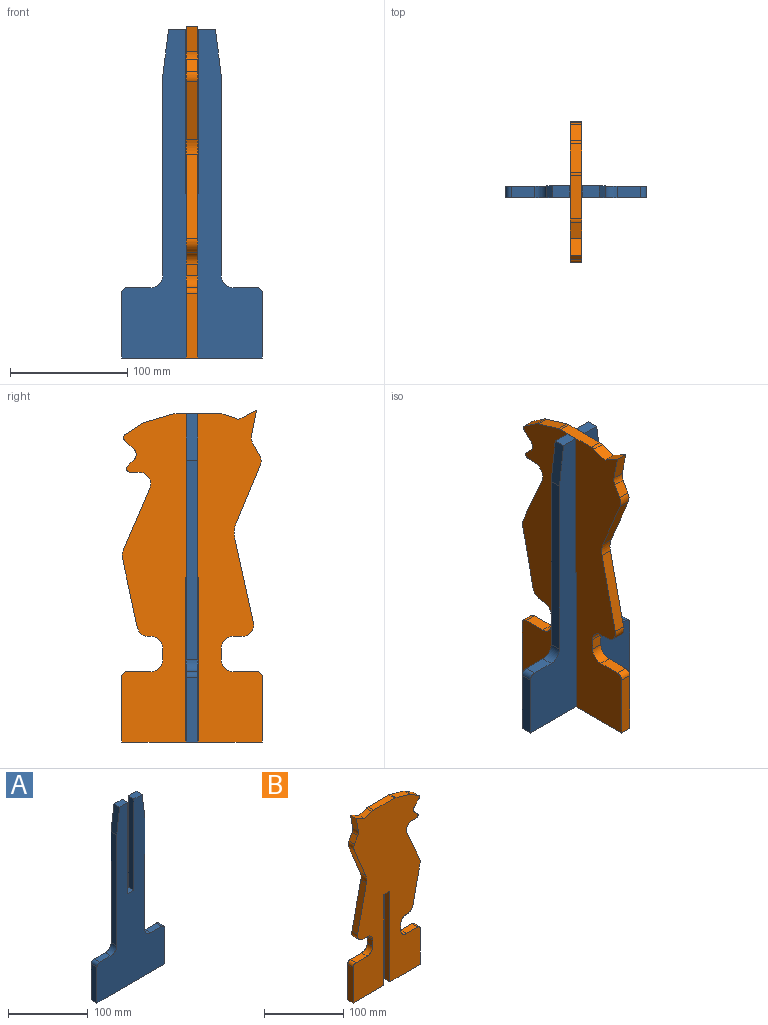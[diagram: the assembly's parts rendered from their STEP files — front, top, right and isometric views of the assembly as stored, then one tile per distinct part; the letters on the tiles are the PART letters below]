
ASSEMBLY  parts=2 mates=1
PART A: 20 faces, bbox 120x10x280 mm
  f0: plane 170x10mm, normal (-1,0,0), area 1700mm2, adj f1,f17,f18,f19
  f1: cylinder r=10mm len=10mm, axis (0,-1,0), area 157.1mm2, adj f0,f2,f18,f19
  f2: plane 20x10mm, normal (0,0,1), area 200mm2, adj f1,f3,f18,f19
  f3: cylinder r=5mm len=10mm, axis (0,-1,0), area 78.5mm2, adj f2,f4,f18,f19
  f4: plane 55x10mm, normal (-1,0,0), area 550mm2, adj f3,f5,f18,f19
  f5: plane 120x10mm, normal (0,0,-1), area 1200mm2, adj f4,f6,f18,f19
  f6: plane 55x10mm, normal (1,0,0), area 550mm2, adj f5,f7,f18,f19
  f7: cylinder r=5mm len=10mm, axis (0,-1,0), area 78.5mm2, adj f6,f8,f18,f19
  f8: plane 20x10mm, normal (0,0,1), area 200mm2, adj f7,f9,f18,f19
  f9: cylinder r=10mm len=10mm, axis (0,-1,0), area 157.1mm2, adj f8,f10,f18,f19
  f10: plane 170x10mm, normal (1,0,0), area 1700mm2, adj f9,f11,f18,f19
  f11: plane 40x10mm, normal (0.99,0,0.12), area 403.1mm2, adj f10,f12,f18,f19
  f12: plane 14.5x10mm, normal (0,0,1), area 145mm2, adj f11,f13,f18,f19
  f13: plane 140x10mm, normal (-1,0,0), area 1400mm2, adj f12,f14,f18,f19
  f14: plane 11x10mm, normal (0,0,1), area 110mm2, adj f13,f15,f18,f19
  f15: plane 140x10mm, normal (1,0,0), area 1400mm2, adj f14,f16,f18,f19
  f16: plane 14.5x10mm, normal (0,0,1), area 145mm2, adj f15,f17,f18,f19
  f17: plane 40x10mm, normal (-0.99,0,0.12), area 403.1mm2, adj f0,f16,f18,f19
  f18: plane 280x120mm, normal (0,1,0), area 16492.2mm2, adj f0,f1,f2,f3,f4,f5,f6,f7
  f19: plane 280x120mm, normal (0,-1,0), area 16492.2mm2, adj f0,f1,f2,f3,f4,f5,f6,f7
PART B: 48 faces, bbox 120x10x283 mm
  f0: cylinder r=10mm len=10mm, axis (0,1,0), area 30mm2, adj f1,f45,f46,f47
  f1: plane 24.16x10mm, normal (0.28,0,0.96), area 252mm2, adj f0,f2,f46,f47
  f2: cylinder r=10mm len=10mm, axis (0,1,0), area 28.8mm2, adj f1,f3,f46,f47
  f3: plane 36.93x10mm, normal (0,0,1), area 369.3mm2, adj f2,f4,f46,f47
  f4: cylinder r=10mm len=10mm, axis (0,1,0), area 32.2mm2, adj f3,f5,f46,f47
  f5: plane 13.46x10mm, normal (-0.32,0,0.95), area 141.9mm2, adj f4,f6,f46,f47
  f6: plane 15x10mm, normal (0.47,0,0.88), area 170mm2, adj f5,f7,f46,f47
  f7: plane 21.4x10mm, normal (-0.98,0,-0.2), area 218.2mm2, adj f6,f8,f46,f47
  f8: cylinder r=10mm len=10mm, axis (0,1,0), area 70.4mm2, adj f7,f9,f46,f47
  f9: plane 10.55x10mm, normal (-0.87,0,0.49), area 120.7mm2, adj f8,f10,f46,f47
  f10: cylinder r=10mm len=10mm, axis (0,1,0), area 90.2mm2, adj f9,f11,f46,f47
  f11: plane 49.68x20.7mm, normal (-0.92,0,-0.38), area 538.2mm2, adj f10,f12,f46,f47
  f12: cylinder r=20mm len=12.03mm, axis (0,1,0), area 122.7mm2, adj f11,f13,f46,f47
  f13: plane 71.65x15.92mm, normal (-0.98,0,0.22), area 733.9mm2, adj f12,f14,f46,f47
  f14: cylinder r=10mm len=12.17mm, axis (0,1,0), area 178.9mm2, adj f13,f15,f46,f47
  f15: plane 10x7.53mm, normal (0,0,-1), area 75.3mm2, adj f14,f16,f46,f47
  f16: cylinder r=10mm len=10mm, axis (0,1,0), area 157.1mm2, adj f15,f17,f46,f47
  f17: plane 10x10mm, normal (-1,0,0), area 100mm2, adj f16,f18,f46,f47
  f18: cylinder r=10mm len=10mm, axis (0,1,0), area 157.1mm2, adj f17,f19,f46,f47
  f19: plane 20x10mm, normal (0,0,1), area 200mm2, adj f18,f20,f46,f47
  f20: cylinder r=5mm len=10mm, axis (0,1,0), area 78.5mm2, adj f19,f21,f46,f47
  f21: plane 55x10mm, normal (-1,0,0), area 550mm2, adj f20,f22,f46,f47
  f22: plane 54.5x10mm, normal (0,0,-1), area 545mm2, adj f21,f23,f46,f47
  f23: plane 140x10mm, normal (1,0,0), area 1400mm2, adj f22,f24,f46,f47
  f24: plane 11x10mm, normal (0,0,-1), area 110mm2, adj f23,f25,f46,f47
  f25: plane 140x10mm, normal (-1,0,0), area 1400mm2, adj f24,f26,f46,f47
  f26: plane 54.5x10mm, normal (0,0,-1), area 545mm2, adj f25,f27,f46,f47
  f27: plane 55x10mm, normal (1,0,0), area 550mm2, adj f26,f28,f46,f47
  f28: cylinder r=5mm len=10mm, axis (0,1,0), area 78.5mm2, adj f27,f29,f46,f47
  f29: plane 20x10mm, normal (0,0,1), area 200mm2, adj f28,f30,f46,f47
  f30: cylinder r=10mm len=10mm, axis (0,1,0), area 157.1mm2, adj f29,f31,f46,f47
  f31: plane 10x10mm, normal (1,0,0), area 100mm2, adj f30,f32,f46,f47
  f32: cylinder r=10mm len=10mm, axis (0,1,0), area 157.1mm2, adj f31,f33,f46,f47
  f33: plane 10x1.92mm, normal (0,0,-1), area 19.2mm2, adj f32,f34,f46,f47
  f34: cylinder r=10mm len=10mm, axis (0,1,0), area 136mm2, adj f33,f35,f46,f47
  f35: plane 58.98x12.64mm, normal (0.98,0,-0.21), area 603.2mm2, adj f34,f36,f46,f47
  f36: cylinder r=10mm len=10mm, axis (0,1,0), area 61.6mm2, adj f35,f37,f46,f47
  f37: plane 53.14x22.77mm, normal (0.92,0,0.39), area 578.1mm2, adj f36,f38,f46,f47
  f38: cylinder r=10mm len=13.94mm, axis (0,1,0), area 197.6mm2, adj f37,f39,f46,f47
  f39: plane 10x7.59mm, normal (0,0,-1), area 75.9mm2, adj f38,f40,f46,f47
  f40: cylinder r=3mm len=10mm, axis (0,1,0), area 70.7mm2, adj f39,f41,f46,f47
  f41: plane 10x5.64mm, normal (0.71,0,0.71), area 79.7mm2, adj f40,f42,f46,f47
  f42: cylinder r=6mm len=10mm, axis (0,1,0), area 94.2mm2, adj f41,f43,f46,f47
  f43: plane 10x8.17mm, normal (0.71,0,-0.71), area 115.5mm2, adj f42,f44,f46,f47
  f44: cylinder r=3mm len=10mm, axis (0,1,0), area 53mm2, adj f43,f45,f46,f47
  f45: plane 13.7x10mm, normal (0.55,0,0.83), area 164.6mm2, adj f0,f44,f46,f47
  f46: plane 283x120mm, normal (0,-1,0), area 25459.4mm2, adj f0,f1,f2,f3,f4,f5,f6,f7
  f47: plane 283x120mm, normal (0,1,0), area 25459.4mm2, adj f0,f1,f2,f3,f4,f5,f6,f7
PLACE A at identity
PLACE B rot(axis=(0,0,1),90deg) t=(-5,5,0)mm
MATE fastened B.f24 <-> A.f14  axis (0,0,-1) through (0,5,110)mm
